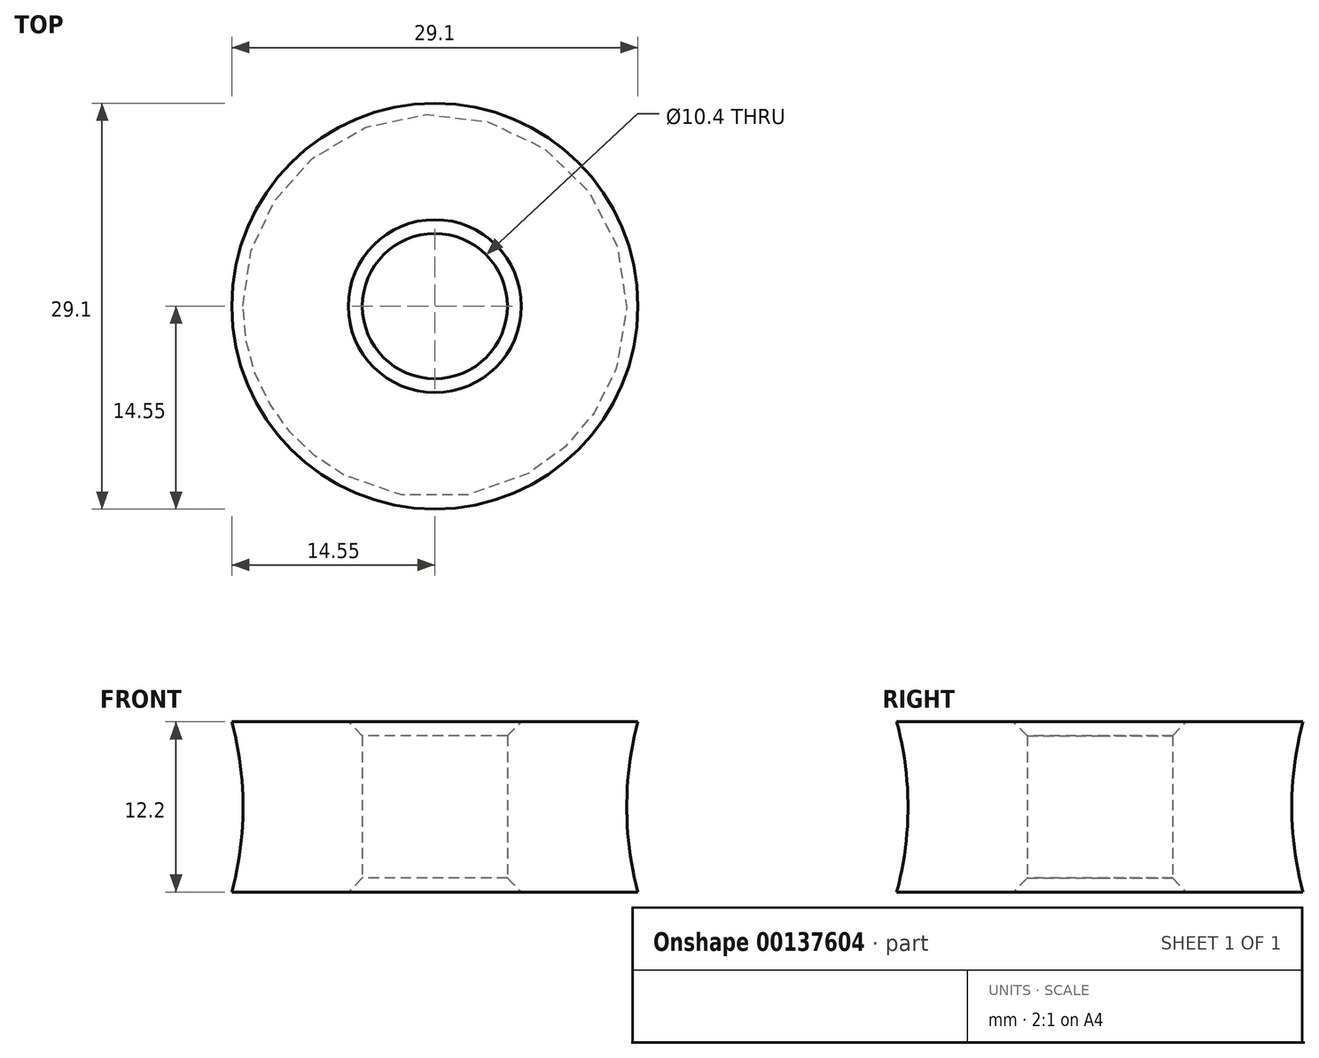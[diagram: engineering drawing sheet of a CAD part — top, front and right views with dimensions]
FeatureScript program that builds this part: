
annotation { "Feature Type Name" : "Feature", "Feature Type Description" : "" }
export const myFeature = defineFeature(function(context is Context, id is Id, definition is map)
    precondition{}
    {
        {
            var Q0;
            Q0=qCreatedBy(makeId("Front.planeOp"),FACE);
            var sketch = newSketch(context, id + "F0", { "sketchPlane" : qUnion([Q0])});
            skLineSegment(sketch, "E0", {"start": v(0, 0) * mm, "end": v(0, 12.2) * mm, "construction": true});
            skLineSegment(sketch, "E1", {"start": v(-14.55, 0) * mm, "end": v(-14.55, 12.2) * mm, "construction": true});
            skLineSegment(sketch, "E2", {"start": v(-13.75, 12.2) * mm, "end": v(-13.75, 0) * mm, "construction": true});
            skPoint(sketch, "E3", {"position": v(-13.75, 6.1) * mm});
            skLineSegment(sketch, "E4", {"start": v(-14.55, 12.2) * mm, "end": v(-5.2, 12.2) * mm});
            skLineSegment(sketch, "E5", {"start": v(-14.55, 0) * mm, "end": v(-5.2, 0) * mm});
            skLineSegment(sketch, "E6", {"start": v(-5.2, 12.2) * mm, "end": v(-5.2, 0) * mm});
            skArc(sketch, "E7", {"start": v(-14.55, 0) * mm, "mid": v(-13.75, 6.1) * mm, "end": v(-14.55, 12.2) * mm});
            skSolve(sketch);
        }
        {
            var Q0;
            Q0=makeQuery(id+"F0.imprint","IMPRINT",FACE,{"disambiguationData":[TD([[makeQuery(id+"F0.imprint","IMPRINT",EDGE,{"derivedFrom":sQuery(id+"F0.wireOp",EDGE,"E4")}),-1.0]])]});
            var Q1;
            Q1=sQuery(id+"F0.wireOp",EDGE,"E0");
            revolve(context, id + "F1", {"entities" : qUnion([Q0]), "axis" : qUnion([Q1]), "revolveType" : RevolveType.FULL});
        }
        {
            var Q0;
            Q0=makeQuery(id+"F1.opRevolve","SWEPT_FACE",FACE,{"disambiguationData":[OSD([sQuery(id+"F0.wireOp",EDGE,"E6")])]});
            chamfer(context, id + "F2", {"entities" : qUnion([Q0]), "width" : 1 * mm, "tangentPropagation" : true});
        }
    });
